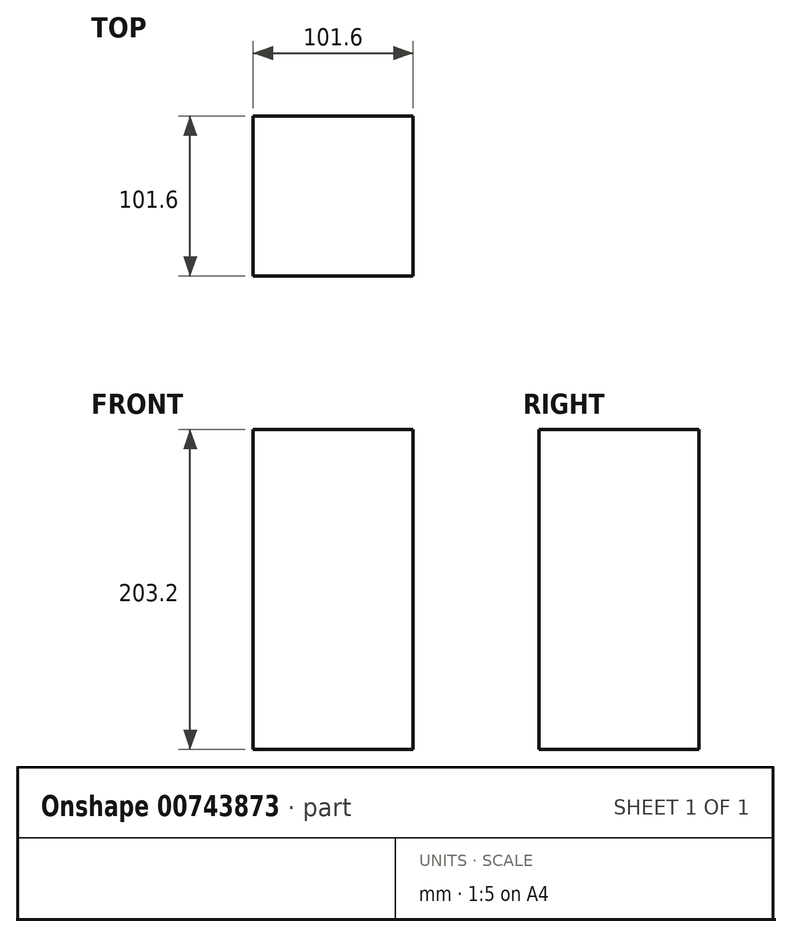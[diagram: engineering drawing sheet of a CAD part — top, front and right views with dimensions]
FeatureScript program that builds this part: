
annotation { "Feature Type Name" : "Feature", "Feature Type Description" : "" }
export const myFeature = defineFeature(function(context is Context, id is Id, definition is map)
    precondition{}
    {
        {
            var Q0;
            Q0=qCreatedBy(makeId("Top.planeOp"),FACE);
            var sketch = newSketch(context, id + "F0", { "sketchPlane" : qUnion([Q0])});
            skLineSegment(sketch, "E0.bottom", {"start": v(0, 0) * mm, "end": v(101.6, 0) * mm});
            skLineSegment(sketch, "E0.top", {"start": v(0, 101.6) * mm, "end": v(101.6, 101.6) * mm});
            skLineSegment(sketch, "E0.left", {"start": v(0, 0) * mm, "end": v(0, 101.6) * mm});
            skLineSegment(sketch, "E0.right", {"start": v(101.6, 0) * mm, "end": v(101.6, 101.6) * mm});
            skSolve(sketch);
        }
        {
            var Q0;
            Q0=makeQuery(id+"F0.imprint","IMPRINT",FACE,{"disambiguationData":[TD([[makeQuery(id+"F0.imprint","IMPRINT",EDGE,{"derivedFrom":sQuery(id+"F0.wireOp",EDGE,"E0.bottom")}),1.0]])]});
            extrude(context, id + "F1", {"entities" : qUnion([Q0]), "depth" : 203.2 * mm, "offsetDistance" : 25.4 * mm});
        }
    });
